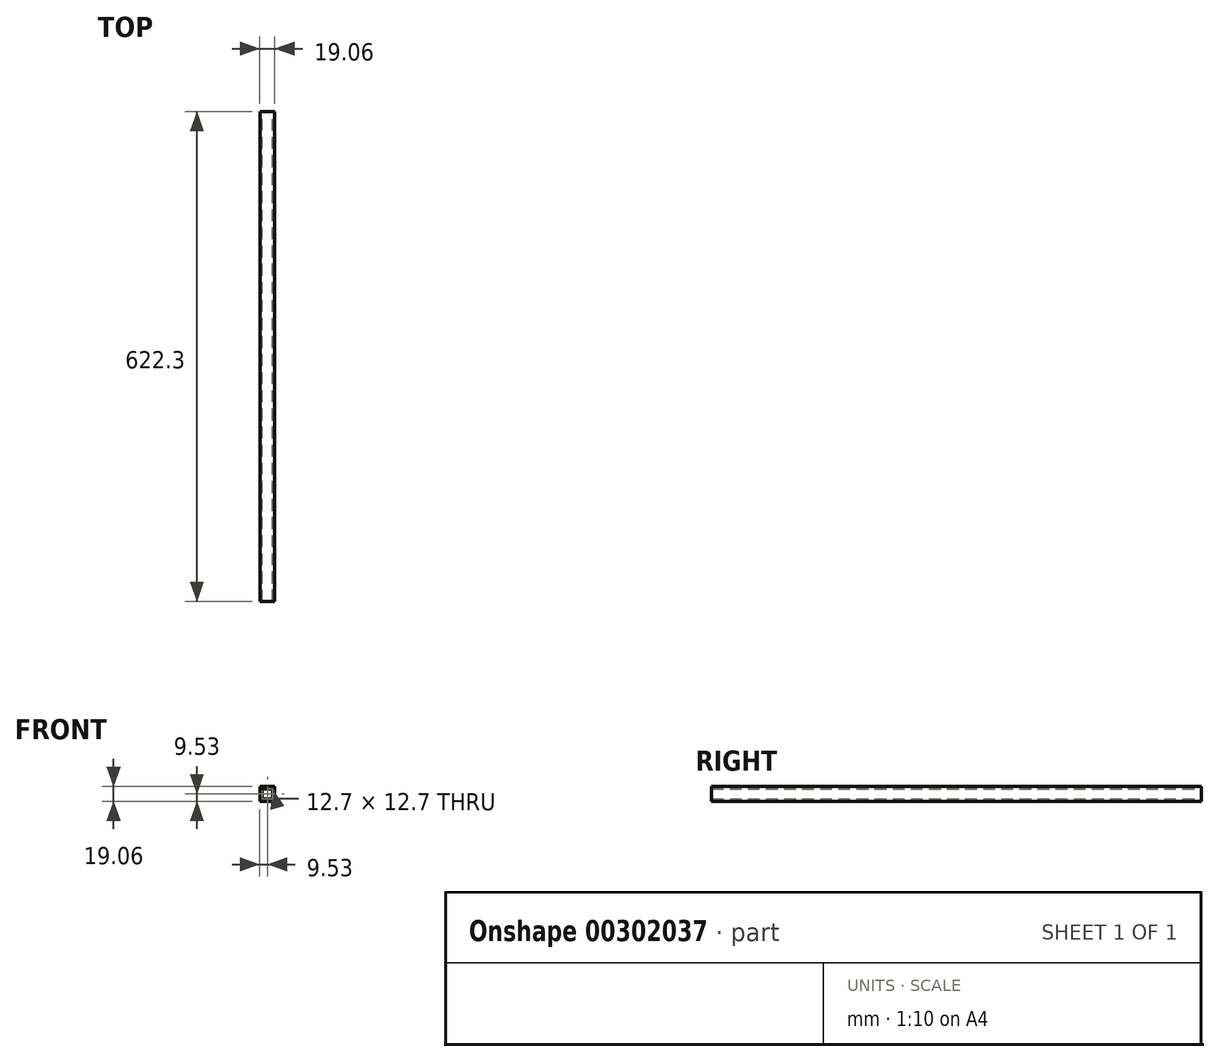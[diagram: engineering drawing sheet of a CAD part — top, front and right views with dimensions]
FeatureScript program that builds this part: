
annotation { "Feature Type Name" : "Feature", "Feature Type Description" : "" }
export const myFeature = defineFeature(function(context is Context, id is Id, definition is map)
    precondition{}
    {
        {
            var Q0;
            Q0=qCreatedBy(makeId("Front.planeOp"),FACE);
            var sketch = newSketch(context, id + "F0", { "sketchPlane" : qUnion([Q0])});
            skLineSegment(sketch, "E0.bottom", {"start": v(9.52, 9.53) * mm, "end": v(-9.53, 9.52) * mm});
            skLineSegment(sketch, "E0.top", {"start": v(9.53, -9.52) * mm, "end": v(-9.52, -9.53) * mm});
            skLineSegment(sketch, "E0.left", {"start": v(9.53, 9.53) * mm, "end": v(9.53, -9.52) * mm});
            skLineSegment(sketch, "E0.right", {"start": v(-9.53, 9.52) * mm, "end": v(-9.53, -9.53) * mm});
            skPoint(sketch, "E0.middle", {"position": v(0, 0) * mm});
            skLineSegment(sketch, "E1.bottom", {"start": v(6.35, 6.35) * mm, "end": v(-6.35, 6.35) * mm});
            skLineSegment(sketch, "E1.top", {"start": v(6.35, -6.35) * mm, "end": v(-6.35, -6.35) * mm});
            skLineSegment(sketch, "E1.left", {"start": v(6.35, 6.35) * mm, "end": v(6.35, -6.35) * mm});
            skLineSegment(sketch, "E1.right", {"start": v(-6.35, 6.35) * mm, "end": v(-6.35, -6.35) * mm});
            skSolve(sketch);
        }
        {
            var Q0;
            Q0 = qSketchRegion(id + "F0", true);
            extrude(context, id + "F1", {"entities" : qUnion([Q0]), "depth" : 622.3 * mm});
        }
    });
